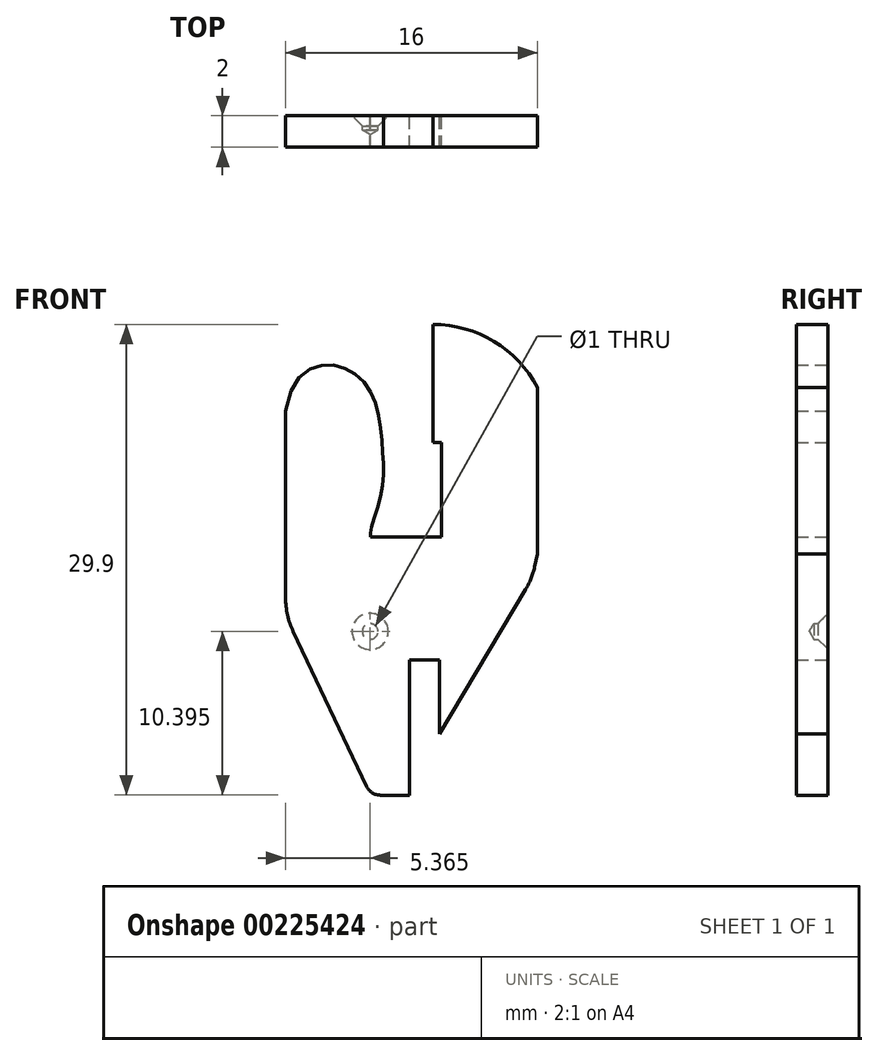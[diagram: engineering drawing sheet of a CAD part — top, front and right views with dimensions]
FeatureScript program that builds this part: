
annotation { "Feature Type Name" : "Feature", "Feature Type Description" : "" }
export const myFeature = defineFeature(function(context is Context, id is Id, definition is map)
    precondition{}
    {
        {
            var Q0;
            Q0=qCreatedBy(makeId("Front.planeOp"),FACE);
            var sketch = newSketch(context, id + "F0", { "sketchPlane" : qUnion([Q0])});
            skLineSegment(sketch, "E0", {"start": v(1.97, -24.86) * mm, "end": v(1.97, -16.26) * mm});
            skLineSegment(sketch, "E1", {"start": v(1.97, -16.26) * mm, "end": v(3.87, -16.26) * mm});
            skLineSegment(sketch, "E2", {"start": v(3.87, -16.26) * mm, "end": v(3.87, -20.98) * mm});
            skLineSegment(sketch, "E3", {"start": v(3.87, -20.98) * mm, "end": v(9.34, -11.8) * mm});
            skLineSegment(sketch, "E4", {"start": v(9.92, -10.36) * mm, "end": v(10.1, -9.55) * mm});
            skLineSegment(sketch, "E5", {"start": v(10.1, -9.55) * mm, "end": v(10.1, 1.03) * mm});
            skLineSegment(sketch, "E6", {"start": v(3.47, 5.04) * mm, "end": v(3.47, -2.46) * mm});
            skLineSegment(sketch, "E7", {"start": v(3.47, -2.46) * mm, "end": v(4, -2.46) * mm});
            skLineSegment(sketch, "E8", {"start": v(4, -2.46) * mm, "end": v(4, -8.46) * mm});
            skLineSegment(sketch, "E9", {"start": v(4, -8.46) * mm, "end": v(-0.5, -8.46) * mm});
            skLineSegment(sketch, "E10", {"start": v(-5.9, -0.45) * mm, "end": v(-5.9, -12.33) * mm});
            skLineSegment(sketch, "E11", {"start": v(-5.41, -14.46) * mm, "end": v(-0.76, -24.3) * mm});
            skLineSegment(sketch, "E12", {"start": v(0.14, -24.86) * mm, "end": v(1.97, -24.86) * mm});
            skFitSpline(sketch, "E13", {"points": [v(-0.5, -8.46) * mm, v(-0.5, -7.99) * mm, v(0.2, -5.57) * mm, v(0.24, -2.74) * mm, v(-0.5, 0.75) * mm, v(-2.94, 2.46) * mm, v(-5.9, -0.45) * mm], "startDerivative": vector(-1.12, 6) * mm, "endDerivative": vector(-4.7, -33.5) * mm});
            skPoint(sketch, "E14.visualSharp", {"position": v(-5.9, -13.45) * mm});
            skArc(sketch, "E14.filletArc", {"start": v(-5.9, -12.33) * mm, "mid": v(-5.77, -13.42) * mm, "end": v(-5.41, -14.46) * mm});
            skPoint(sketch, "E15.visualSharp", {"position": v(9.75, -11.12) * mm});
            skArc(sketch, "E15.filletArc", {"start": v(9.34, -11.8) * mm, "mid": v(9.69, -11.1) * mm, "end": v(9.92, -10.36) * mm});
            skArc(sketch, "E16", {"start": v(3.47, 5.04) * mm, "mid": v(7.35, 3.96) * mm, "end": v(10.1, 1.03) * mm});
            skPoint(sketch, "E17", {"position": v(-0.53, -14.46) * mm});
            skPoint(sketch, "E18.visualSharp", {"position": v(-0.5, -24.86) * mm});
            skArc(sketch, "E18.filletArc", {"start": v(-0.76, -24.3) * mm, "mid": v(-0.4, -24.7) * mm, "end": v(0.14, -24.86) * mm});
            skSolve(sketch);
        }
        {
            var Q0;
            Q0 = qSketchRegion(id + "F0", true);
            extrude(context, id + "F1", {"entities" : qUnion([Q0]), "depth" : 2 * mm});
        }
        {
            var Q0;
            Q0=sQuery(id+"F0.wireOp",VERTEX,"E17");
            var Q1;
            Q1=makeQuery(id+"F1.opExtrude","SWEPT_BODY",BODY,{"disambiguationData":[OSD([sQuery(id+"F0.wireOp",EDGE,"E0"),sQuery(id+"F0.wireOp",EDGE,"E1"),sQuery(id+"F0.wireOp",EDGE,"E2"),sQuery(id+"F0.wireOp",EDGE,"E3"),sQuery(id+"F0.wireOp",EDGE,"E4"),sQuery(id+"F0.wireOp",EDGE,"E5"),sQuery(id+"F0.wireOp",EDGE,"E6"),sQuery(id+"F0.wireOp",EDGE,"E7"),sQuery(id+"F0.wireOp",EDGE,"E8"),sQuery(id+"F0.wireOp",EDGE,"E9"),sQuery(id+"F0.wireOp",EDGE,"E10"),sQuery(id+"F0.wireOp",EDGE,"E11"),sQuery(id+"F0.wireOp",EDGE,"E12"),sQuery(id+"F0.wireOp",EDGE,"E13"),sQuery(id+"F0.wireOp",EDGE,"E14.filletArc"),sQuery(id+"F0.wireOp",EDGE,"E15.filletArc"),sQuery(id+"F0.wireOp",EDGE,"E16"),sQuery(id+"F0.wireOp",EDGE,"E18.filletArc")])]});
            hole(context, id + "F2", {"style" : HoleStyle.C_SINK, "endStyle" : HoleEndStyle.BLIND, "oppositeDirection" : true, "holeDiameter" : 1 * mm, "cSinkDiameter" : 2.3 * mm, "cSinkAngle" : 90 * degree, "holeDepth" : 0.9 * mm, "startFromSketch" : true, "locations" : qUnion([Q0]), "scope" : qUnion([Q1])});
        }
    });
